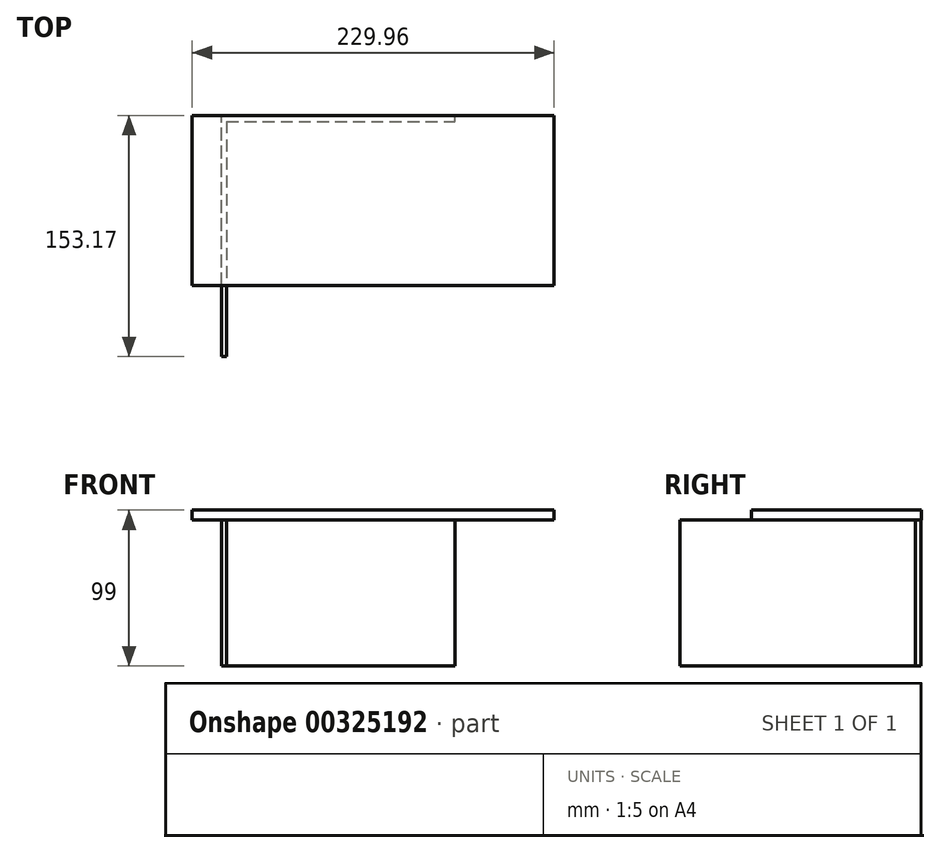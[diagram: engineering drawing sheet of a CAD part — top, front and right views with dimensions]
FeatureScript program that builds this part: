
annotation { "Feature Type Name" : "Feature", "Feature Type Description" : "" }
export const myFeature = defineFeature(function(context is Context, id is Id, definition is map)
    precondition{}
    {
        {
            var Q0;
            Q0=qCreatedBy(makeId("Top.planeOp"),FACE);
            var sketch = newSketch(context, id + "F0", { "sketchPlane" : qUnion([Q0])});
            skLineSegment(sketch, "E0.bottom", {"start": v(-73.62, 72.32) * mm, "end": v(74.49, 72.32) * mm});
            skLineSegment(sketch, "E0.top", {"start": v(-73.62, 75.79) * mm, "end": v(74.49, 75.79) * mm});
            skLineSegment(sketch, "E0.left", {"start": v(-73.62, 72.32) * mm, "end": v(-73.62, 75.79) * mm});
            skLineSegment(sketch, "E0.right", {"start": v(74.49, 72.32) * mm, "end": v(74.49, 75.79) * mm});
            skLineSegment(sketch, "E1.bottom", {"start": v(-73.62, 72.32) * mm, "end": v(-70.49, 72.32) * mm});
            skLineSegment(sketch, "E1.top", {"start": v(-73.62, -77.09) * mm, "end": v(-70.49, -77.09) * mm});
            skLineSegment(sketch, "E1.left", {"start": v(-73.62, 72.32) * mm, "end": v(-73.62, -77.09) * mm});
            skLineSegment(sketch, "E1.right", {"start": v(-70.49, 72.32) * mm, "end": v(-70.49, -77.09) * mm});
            skSolve(sketch);
        }
        {
            var Q0;
            Q0 = qSketchRegion(id + "F0", true);
            extrude(context, id + "F1", {"entities" : qUnion([Q0]), "oppositeDirection" : true, "depth" : 92.76 * mm});
        }
        {
            var Q0;
            Q0=qCreatedBy(makeId("Top.planeOp"),FACE);
            var sketch = newSketch(context, id + "F2", { "sketchPlane" : qUnion([Q0])});
            skLineSegment(sketch, "E2.bottom", {"start": v(-92.32, 76.08) * mm, "end": v(137.64, 76.08) * mm});
            skLineSegment(sketch, "E2.top", {"start": v(-92.32, -31.89) * mm, "end": v(137.64, -31.89) * mm});
            skLineSegment(sketch, "E2.left", {"start": v(137.64, 76.08) * mm, "end": v(137.64, -31.89) * mm});
            skLineSegment(sketch, "E2.right", {"start": v(-92.32, 76.08) * mm, "end": v(-92.32, -31.89) * mm});
            skSolve(sketch);
        }
        {
            var Q0;
            Q0 = qSketchRegion(id + "F2", true);
            extrude(context, id + "F3", {"entities" : qUnion([Q0]), "operationType" : NewBodyOperationType.ADD, "depth" : 6.24 * mm});
        }
    });
